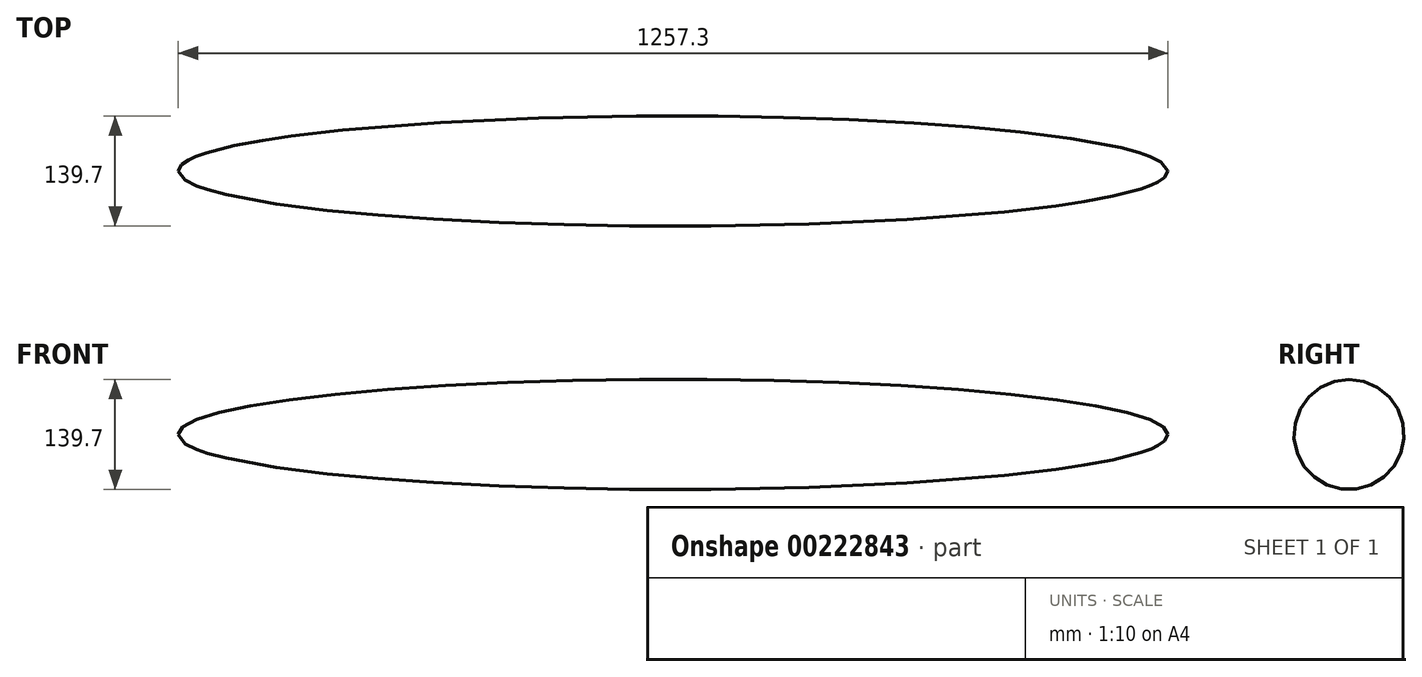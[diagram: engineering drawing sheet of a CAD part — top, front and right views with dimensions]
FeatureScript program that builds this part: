
annotation { "Feature Type Name" : "Feature", "Feature Type Description" : "" }
export const myFeature = defineFeature(function(context is Context, id is Id, definition is map)
    precondition{}
    {
        {
            assignVariable(context, id + "F0", {"name" : "diameter", "anyValue" : 139.7 * mm});
        }
        {
            var Q0;
            Q0=qCreatedBy(makeId("Front.planeOp"),FACE);
            var sketch = newSketch(context, id + "F1", { "sketchPlane" : qUnion([Q0])});
            skLineSegment(sketch, "E0", {"start": v(0, 0) * mm, "end": v(0, 69.85) * mm, "construction": true});
            skLineSegment(sketch, "E1", {"start": v(0, 0) * mm, "end": v(-628.65, 0) * mm, "construction": true});
            skEllipticalArc(sketch, "E2", {});
            skLineSegment(sketch, "E3", {"start": v(-628.65, 0) * mm, "end": v(628.65, 0) * mm});
            const initialGuessF1  = {"E2": [0, 0, -1, 0, 0.62865, 0.06985, 3.141592653589793, 0]};
            skSetInitialGuess(sketch, initialGuessF1);
            skSolve(sketch);
        }
        {
            var Q0;
            Q0 = qSketchRegion(id + "F1", true);
            var Q1;
            Q1=sQuery(id+"F1.wireOp",EDGE,"E1");
            revolve(context, id + "F2", {"entities" : qUnion([Q0]), "axis" : qUnion([Q1]), "revolveType" : RevolveType.FULL});
        }
        {
            var Q0;
            Q0=makeQuery(id+"F2.opRevolve","SWEPT_BODY",BODY,{"disambiguationData":[OSD([sQuery(id+"F1.wireOp",EDGE,"E2"),sQuery(id+"F1.wireOp",EDGE,"E3")])]});
            transform(context, id + "F3", {"entities" : qUnion([Q0]), "transformType" : TransformType.TRANSLATION_3D, "dx" : getVariable(context, 'diameter') * 9 / 2 - getVariable(context, 'diameter'), "dy" : 0 * mm, "dz" : 0 * mm, "makeCopy" : false});
        }
    });
